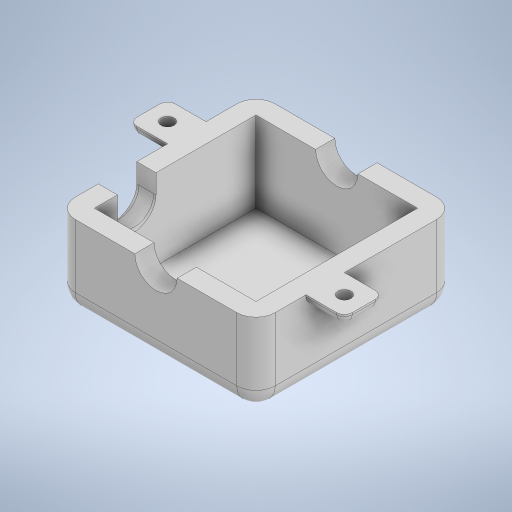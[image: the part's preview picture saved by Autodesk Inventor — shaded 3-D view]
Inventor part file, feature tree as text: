
AUTODESK INVENTOR PART (.ipt)
format: ipt  version: 2023.2 (Build 272271000, 271)  size: 512,000 bytes
history: native  units: mm
features: sketch x14, extrude x12, fillet x10, hole x2, other x1
ambient origin geometry x8: Origin, YZ Plane, XZ Plane, XY Plane, X Axis, Y Axis, Z Axis, Center Point
bodies: Solid1 (feature_tree)
feature tree (39):
  extrude  "Extrusion1"  Depth=30.0mm
  hole  "Hole1"  [1 undecoded]
  extrude  "Extrusion2"  Depth=2.0mm
  extrude  "Extrusion3"  Depth=5.0mm
  extrude  "Extrusion4"  Depth=2.0mm
  extrude  "Extrusion6"  Depth=15.0mm TaperAngle=0.0deg
  extrude  "Extrusion7"  Depth=0.5mm
  extrude  "Extrusion8"  Depth=15.0mm
  extrude  "Extrusion9"  Depth=16.0mm TaperAngle=0.0deg
  extrude  "Extrusion10"  Depth=5.0mm TaperAngle=0.0deg
  fillet  "Face Fillet1"
  fillet  "Face Fillet2"
  other  "Full Round Fillet1"
  fillet  "Face Fillet9"
  fillet  "Face Fillet10"
  fillet  "Face Fillet11"
  fillet  "Face Fillet12"
  fillet  "Face Fillet13"
  fillet  "Face Fillet14"
  fillet  "Fillet1"  Radius=5.0mm
  extrude  "Extrusion11"  Depth=5.0mm
  extrude  "Extrusion12"  Depth=5.0mm
  hole  "Hole2"  [1 undecoded]
  fillet  "Fillet2"  Radius=5.0mm
  extrude  "Extrusion13"  Depth=10.0mm
  sketch  "Sketch1"  dims[d0=20.0mm d1=30.0mm]
  sketch  "Sketch2"  dims[d2=12.0mm d3=12.0mm]
  sketch  "Sketch3"  dims[d4=9.827949mm d5=2.0mm]
  sketch  "Sketch5"  dims[d6=5.0mm d7=0.0mm d8=12.0mm]
  sketch  "Sketch6"  dims[d9=9.827949mm]
  sketch  "Sketch11"  dims[d10=3.4mm d11=6.0mm d12=6.3mm d13=2.0mm d14=90.0deg d15=8.0mm d16=20.594885mm d17=20.0mm]
  sketch  "Sketch12"  dims[d18=15.0mm d19=15.0mm d20=0.0mm]
  sketch  "Sketch13"  dims[d21=15.0mm d22=0.5mm]
  sketch  "Sketch14"  dims[d23=16.0mm d24=0.0mm d25=15.0mm]
  sketch  "Sketch15"  dims[d26=0.5mm d27=16.0mm d28=0.0mm]
  sketch  "Sketch16"  dims[d31=18.5mm d32=0.0mm d33=18.5mm d34=0.0mm d35=5.0mm]
  sketch  "Sketch17"  dims[d36=5.0mm d37=42.0mm]
  sketch  "Sketch18"  dims[d38=42.0mm d39=5.0mm]
  sketch  "Sketch19"  dims[d40=21.0mm d41=0.0mm d42=5.0mm d43=5.0mm d44=21.0mm d45=5.0mm d46=15.0mm d47=20.0mm d49=1.0mm d50=5.0mm d51=10.0mm d52=5.0mm d53=10.0mm d54=5.0mm d55=21.0mm d56=0.0mm d57=1.5mm d58=5.0mm d60=0.0mm d61=0.0mm d62=0.589mm d63=0.589mm d70=5.0mm d71=5.0mm d72=5.0mm d73=5.0mm d74=5.0mm d75=5.0mm d76=2.0mm d77=11.0mm d78=8.0mm d79=10.0mm d80=2.5mm d81=10.0mm d82=0.0mm d83=8.0mm d84=10.0mm d85=2.5mm d86=10.0mm d87=0.0mm d88=3.4mm d89=6.0mm d90=4.0mm d91=2.0mm d92=90.0deg d93=8.0mm d94=20.594885mm d95=2.0mm d96=10.0mm d97=0.0mm d98=0.5mm d99=0.872665mm]
note: 2 required parameter values undecoded (feature->parameter linkage not recoverable at this tier; creation-order binding heuristic only, values carry confidence <= 0.55)
